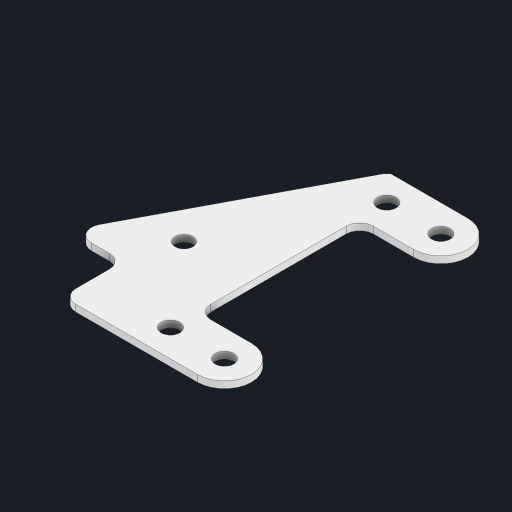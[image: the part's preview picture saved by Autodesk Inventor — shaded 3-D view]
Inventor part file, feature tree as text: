
AUTODESK INVENTOR PART (.ipt)
format: ipt  version: 2024 (Build 280153000, 153)  size: 164,864 bytes
history: native  units: in
note: dims shown in document units (in); Inventor stores cm internally (conversion verified against a paired STEP export)
features: other x5, extrude x1, fillet x1, sketch x1
ambient origin geometry x8: Origin, YZ Plane, XZ Plane, XY Plane, X Axis, Y Axis, Z Axis, Center Point
bodies: Solid1 (feature_tree)
feature tree (8):
  other  "gusset.ipt"
  other  "Blocks"
  extrude  "Extrusion2"  Depth=0.125in
  fillet  "Fillet1"  Radius=0.3937in
  other  "main"
  other  "Solid1::gusset.ipt"
  other  "TaggingFeature1"
  sketch  "Sketch2"  dims[d0=0.125in d3=0.125in d4=0.3937in d5=1.0in d6=0.0in d7=0.125in]
